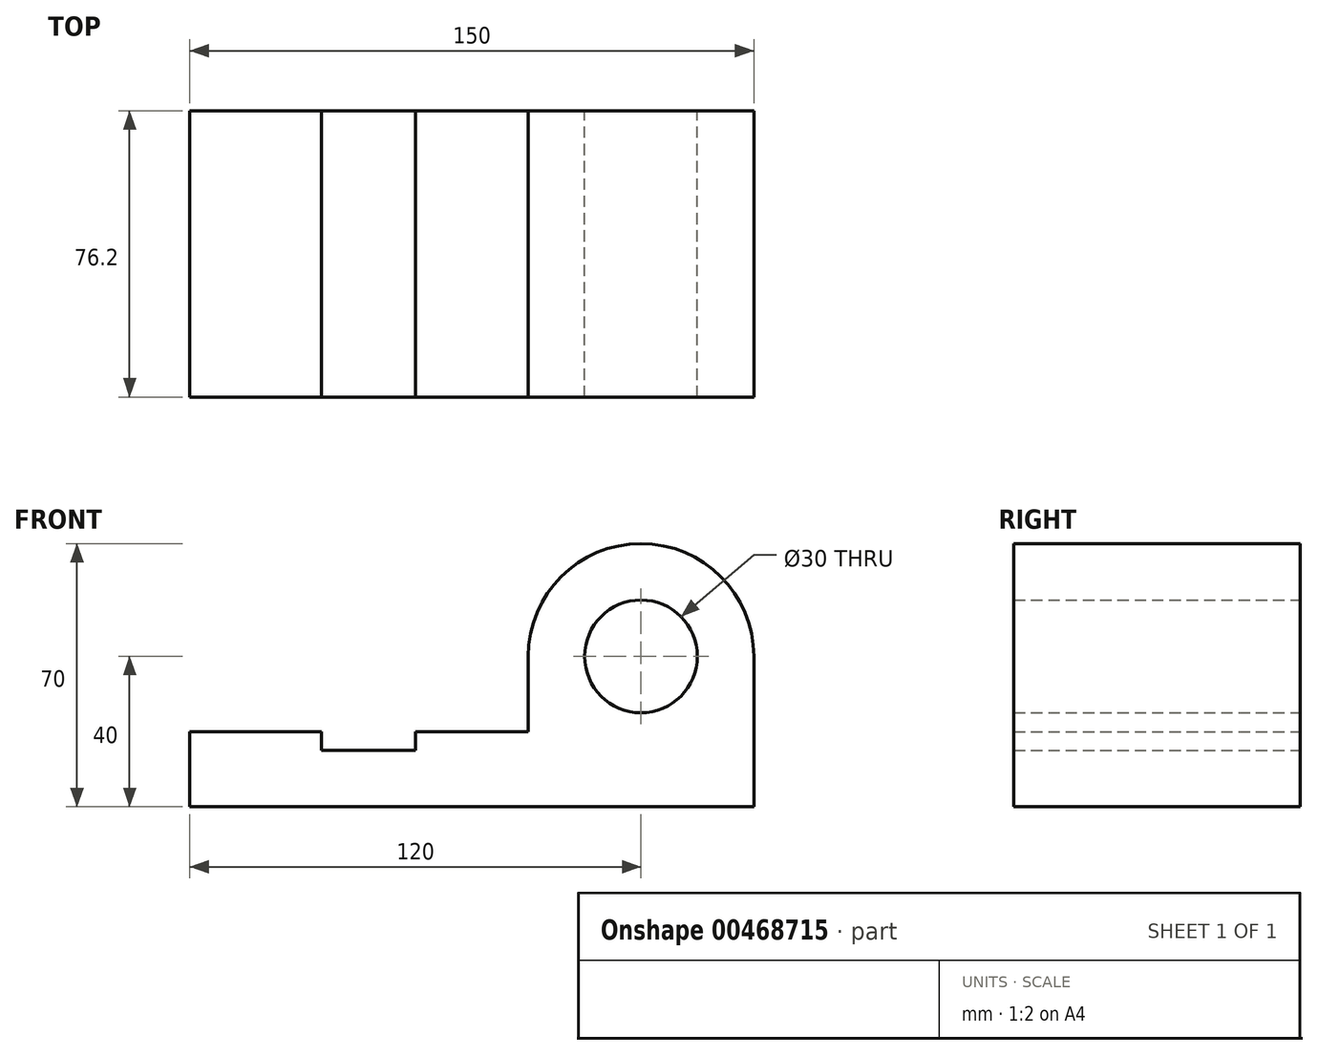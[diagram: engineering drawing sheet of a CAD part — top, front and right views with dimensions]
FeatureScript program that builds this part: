
annotation { "Feature Type Name" : "Feature", "Feature Type Description" : "" }
export const myFeature = defineFeature(function(context is Context, id is Id, definition is map)
    precondition{}
    {
        {
            var Q0;
            Q0=qCreatedBy(makeId("Front.planeOp"),FACE);
            var sketch = newSketch(context, id + "F0", { "sketchPlane" : qUnion([Q0])});
            skLineSegment(sketch, "E0", {"start": v(0, 0) * mm, "end": v(150, 0) * mm});
            skLineSegment(sketch, "E1", {"start": v(0, 0) * mm, "end": v(0, 20) * mm});
            skLineSegment(sketch, "E2", {"start": v(0, 20) * mm, "end": v(35, 20) * mm});
            skLineSegment(sketch, "E3", {"start": v(35, 20) * mm, "end": v(35, 15) * mm});
            skLineSegment(sketch, "E4", {"start": v(35, 15) * mm, "end": v(60, 15) * mm});
            skLineSegment(sketch, "E5", {"start": v(60, 15) * mm, "end": v(60, 20) * mm});
            skLineSegment(sketch, "E6", {"start": v(60, 20) * mm, "end": v(90, 20) * mm});
            skLineSegment(sketch, "E7", {"start": v(150, 0) * mm, "end": v(150, 40) * mm});
            skArc(sketch, "E8", {"start": v(150, 40) * mm, "mid": v(120, 70) * mm, "end": v(90, 40) * mm});
            skLineSegment(sketch, "E9", {"start": v(90, 20) * mm, "end": v(90, 40) * mm});
            skCircle(sketch, "E10", {"center": v(120, 40) * mm, "radius": 15 * mm});
            skSolve(sketch);
        }
        {
            var Q0;
            Q0=makeQuery(id+"F0.imprint","IMPRINT",FACE,{"disambiguationData":[TD([[makeQuery(id+"F0.imprint","IMPRINT",EDGE,{"derivedFrom":sQuery(id+"F0.wireOp",EDGE,"E0")}),1.0]])]});
            extrude(context, id + "F1", {"entities" : qUnion([Q0]), "depth" : 76.2 * mm});
        }
    });
